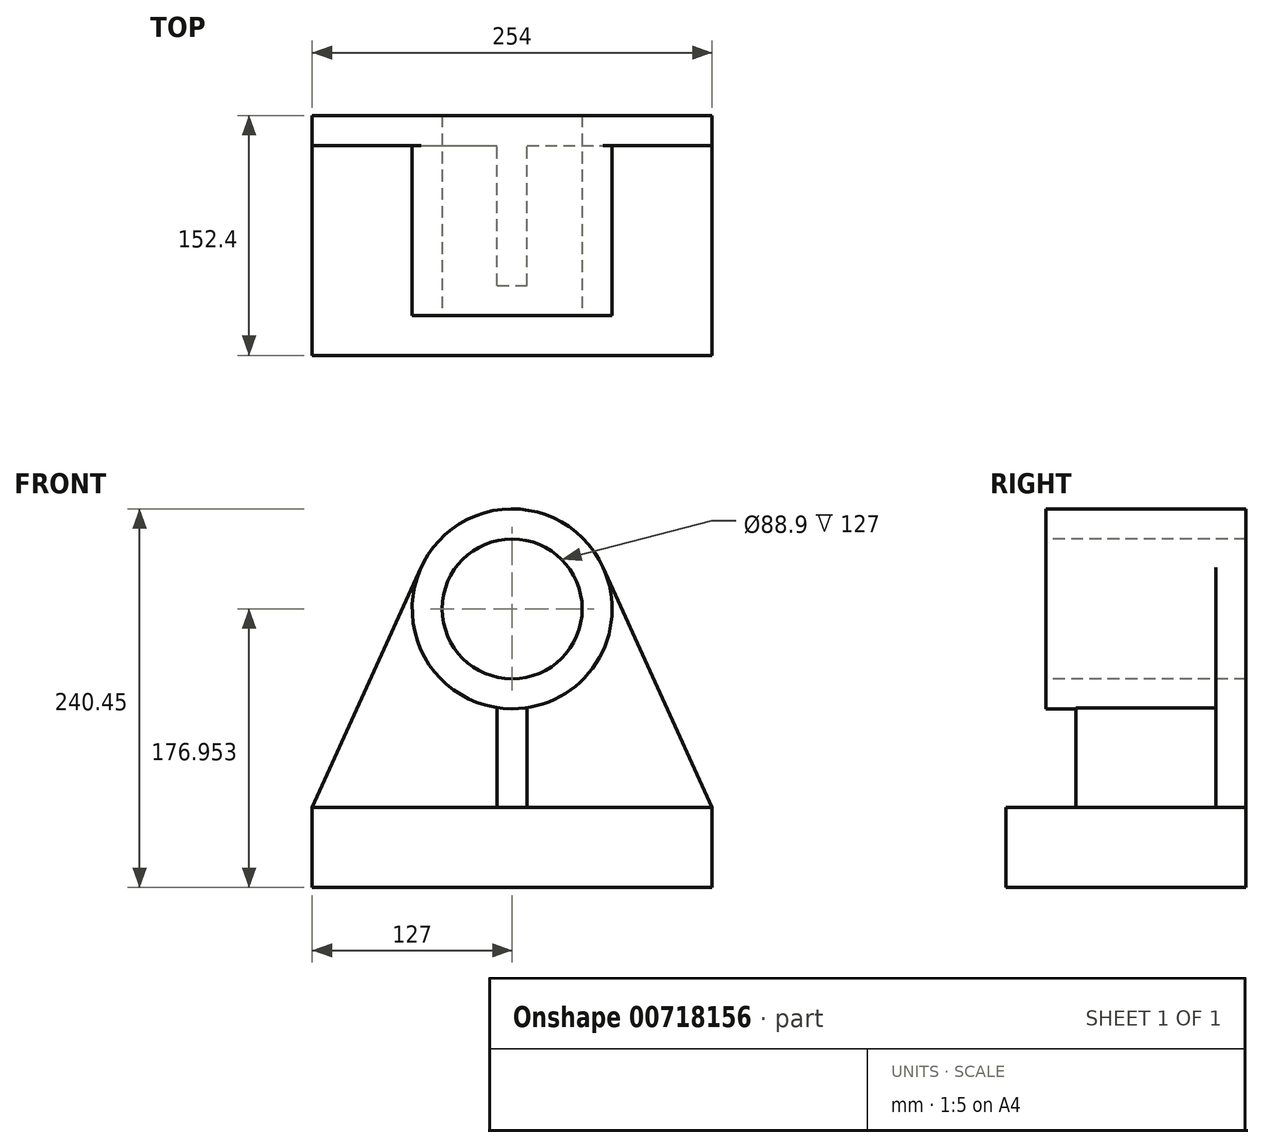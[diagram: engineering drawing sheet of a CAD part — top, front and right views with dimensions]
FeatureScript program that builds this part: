
annotation { "Feature Type Name" : "Feature", "Feature Type Description" : "" }
export const myFeature = defineFeature(function(context is Context, id is Id, definition is map)
    precondition{}
    {
        {
            var Q0;
            Q0=qCreatedBy(makeId("Front.planeOp"),FACE);
            var sketch = newSketch(context, id + "F0", { "sketchPlane" : qUnion([Q0])});
            skLineSegment(sketch, "E0.bottom", {"start": v(0, 0) * mm, "end": v(254, 0) * mm});
            skLineSegment(sketch, "E0.left", {"start": v(0, 0) * mm, "end": v(0, 50.8) * mm});
            skLineSegment(sketch, "E0.right", {"start": v(254, 0) * mm, "end": v(254, 50.8) * mm});
            skLineSegment(sketch, "E1", {"start": v(0, 50.8) * mm, "end": v(69.18, 203.2) * mm});
            skLineSegment(sketch, "E2", {"start": v(254, 50.8) * mm, "end": v(184.82, 203.2) * mm});
            skArc(sketch, "E3", {"start": v(184.82, 203.2) * mm, "mid": v(127, 240.45) * mm, "end": v(69.18, 203.2) * mm});
            skSolve(sketch);
        }
        {
            var Q0;
            Q0=makeQuery(id+"F0.imprint","IMPRINT",FACE,{"disambiguationData":[TD([[makeQuery(id+"F0.imprint","IMPRINT",EDGE,{"derivedFrom":sQuery(id+"F0.wireOp",EDGE,"E0.bottom")}),1.0]])]});
            extrude(context, id + "F1", {"entities" : qUnion([Q0]), "depth" : 19.05 * mm, "offsetDistance" : 25.4 * mm});
        }
        {
            var Q0;
            Q0=makeQuery(id+"F1.opExtrude","CAP_FACE",FACE,{"disambiguationData":[OSD([sQuery(id+"F0.wireOp",EDGE,"E0.bottom"),sQuery(id+"F0.wireOp",EDGE,"E0.left"),sQuery(id+"F0.wireOp",EDGE,"E0.right"),sQuery(id+"F0.wireOp",EDGE,"E1"),sQuery(id+"F0.wireOp",EDGE,"E2"),sQuery(id+"F0.wireOp",EDGE,"E3")])],"isStart":false});
            var sketch = newSketch(context, id + "F2", { "sketchPlane" : qUnion([Q0])});
            skLineSegment(sketch, "E4.bottom", {"start": v(0, 0) * mm, "end": v(254, 0) * mm});
            skLineSegment(sketch, "E4.top", {"start": v(0, 50.8) * mm, "end": v(254, 50.8) * mm});
            skLineSegment(sketch, "E4.left", {"start": v(0, 0) * mm, "end": v(0, 50.8) * mm});
            skLineSegment(sketch, "E4.right", {"start": v(254, 0) * mm, "end": v(254, 50.8) * mm});
            skSolve(sketch);
        }
        {
            var Q0;
            Q0=makeQuery(id+"F2.imprint","IMPRINT",FACE,{"disambiguationData":[TD([[makeQuery(id+"F2.imprint","IMPRINT",EDGE,{"derivedFrom":sQuery(id+"F2.wireOp",EDGE,"E4.bottom")}),1.0]])]});
            extrude(context, id + "F3", {"entities" : qUnion([Q0]), "operationType" : NewBodyOperationType.ADD, "depth" : 133.35 * mm, "offsetDistance" : 25.4 * mm});
        }
        {
            var Q0;
            Q0=makeQuery(id+"F1.opExtrude","CAP_FACE",FACE,{"disambiguationData":[OSD([sQuery(id+"F0.wireOp",EDGE,"E0.bottom"),sQuery(id+"F0.wireOp",EDGE,"E0.left"),sQuery(id+"F0.wireOp",EDGE,"E0.right"),sQuery(id+"F0.wireOp",EDGE,"E1"),sQuery(id+"F0.wireOp",EDGE,"E2"),sQuery(id+"F0.wireOp",EDGE,"E3")])],"isStart":false});
            var sketch = newSketch(context, id + "F4", { "sketchPlane" : qUnion([Q0])});
            skCircle(sketch, "E5", {"center": v(127, 176.95) * mm, "radius": 63.5 * mm});
            skSolve(sketch);
        }
        {
            var Q0;
            Q0=makeQuery(id+"F1.opExtrude","CAP_FACE",FACE,{"disambiguationData":[OSD([sQuery(id+"F0.wireOp",EDGE,"E0.bottom"),sQuery(id+"F0.wireOp",EDGE,"E0.left"),sQuery(id+"F0.wireOp",EDGE,"E0.right"),sQuery(id+"F0.wireOp",EDGE,"E1"),sQuery(id+"F0.wireOp",EDGE,"E2"),sQuery(id+"F0.wireOp",EDGE,"E3")])],"isStart":false});
            var sketch = newSketch(context, id + "F5", { "sketchPlane" : qUnion([Q0])});
            skCircle(sketch, "E6", {"center": v(127, 176.95) * mm, "radius": 44.45 * mm});
            skSolve(sketch);
        }
        {
            var Q0;
            Q0=qSketchRegion(id+"F5",true);
            extrude(context, id + "F6", {"entities" : qUnion([Q0]), "operationType" : NewBodyOperationType.REMOVE, "endBound" : BoundingType.THROUGH_ALL, "oppositeDirection" : true, "depth" : 25.4 * mm, "offsetDistance" : 25.4 * mm});
        }
        {
            var Q0;
            {var subQ0=sQuery(id+"F4.wireOp",EDGE,"E5");var subQ1=makeQuery(id+"F4.imprint","INTERSECT",VERTEX,{"derivedFrom":[makeQuery(id+"F1.opExtrude","CAP_EDGE",EDGE,{"disambiguationData":[OSD([sQuery(id+"F0.wireOp",EDGE,"E1")])],"isStart":false}),subQ0]});Q0=makeQuery(id+"F4.imprint","IMPRINT",FACE,{"disambiguationData":[TD([[makeQuery(id+"F4.imprint","IMPRINT",EDGE,{"disambiguationData":[TD([[subQ1,1.0]])],"derivedFrom":subQ0}),1.0]])]});}
            extrude(context, id + "F7", {"entities" : qUnion([Q0]), "operationType" : NewBodyOperationType.ADD, "depth" : 107.95 * mm, "offsetDistance" : 25.4 * mm});
        }
        {
            var Q0;
            Q0=qSketchRegion(id+"F5",true);
            extrude(context, id + "F8", {"entities" : qUnion([Q0]), "operationType" : NewBodyOperationType.REMOVE, "endBound" : BoundingType.THROUGH_ALL, "depth" : 25.4 * mm, "offsetDistance" : 25.4 * mm, "hasSecondDirection" : true, "secondDirectionBound" : SecondDirectionBoundingType.THROUGH_ALL, "secondDirectionOppositeDirection" : true, "secondDirectionDepth" : 25.4 * mm});
        }
        {
            var Q0;
            Q0=makeQuery(id+"F1.opExtrude","CAP_FACE",FACE,{"disambiguationData":[OSD([sQuery(id+"F0.wireOp",EDGE,"E0.bottom"),sQuery(id+"F0.wireOp",EDGE,"E0.left"),sQuery(id+"F0.wireOp",EDGE,"E0.right"),sQuery(id+"F0.wireOp",EDGE,"E1"),sQuery(id+"F0.wireOp",EDGE,"E2"),sQuery(id+"F0.wireOp",EDGE,"E3")])],"isStart":false});
            var sketch = newSketch(context, id + "F9", { "sketchPlane" : qUnion([Q0])});
            skLineSegment(sketch, "E7.bottom", {"start": v(117.48, 50.8) * mm, "end": v(136.53, 50.8) * mm});
            skLineSegment(sketch, "E7.left", {"start": v(117.48, 50.8) * mm, "end": v(117.48, 114.17) * mm});
            skLineSegment(sketch, "E7.right", {"start": v(136.53, 50.8) * mm, "end": v(136.53, 114.17) * mm});
            skArc(sketch, "E8", {"start": v(117.48, 114.17) * mm, "mid": v(127, 113.45) * mm, "end": v(136.53, 114.17) * mm});
            skLineSegment(sketch, "E9", {"start": v(127, 113.45) * mm, "end": v(127, 50.8) * mm, "construction": true});
            skPoint(sketch, "E9.startSnap0", {"position": v(127, 113.45) * mm});
            skSolve(sketch);
        }
        {
            var Q0;
            Q0=qSketchRegion(id+"F9",true);
            extrude(context, id + "F10", {"entities" : qUnion([Q0]), "operationType" : NewBodyOperationType.ADD, "depth" : 88.9 * mm, "offsetDistance" : 25.4 * mm});
        }
    });
